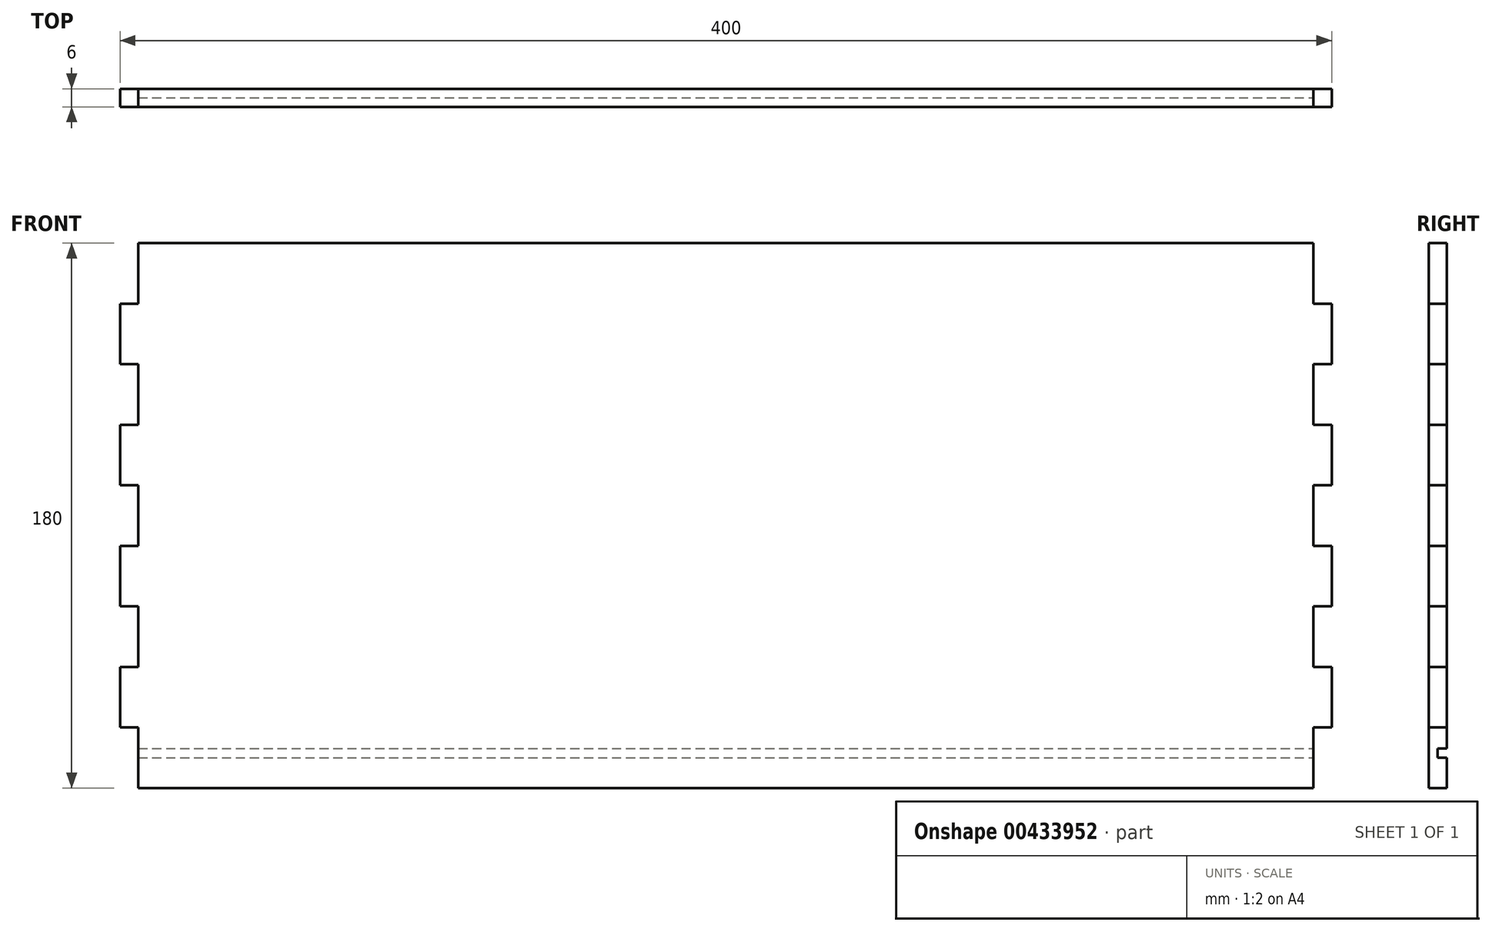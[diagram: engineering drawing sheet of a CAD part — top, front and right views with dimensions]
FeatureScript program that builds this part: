
annotation { "Feature Type Name" : "Feature", "Feature Type Description" : "" }
export const myFeature = defineFeature(function(context is Context, id is Id, definition is map)
    precondition{}
    {
        {
            var Q0;
            Q0=qCreatedBy(makeId("Top.planeOp"),FACE);
            var sketch = newSketch(context, id + "F0", { "sketchPlane" : qUnion([Q0])});
            skLineSegment(sketch, "E0.bottom", {"start": v(200, -3) * mm, "end": v(-200, -3) * mm});
            skLineSegment(sketch, "E0.top", {"start": v(200, 3) * mm, "end": v(-200, 3) * mm});
            skLineSegment(sketch, "E0.left", {"start": v(200, -3) * mm, "end": v(200, 3) * mm});
            skLineSegment(sketch, "E0.right", {"start": v(-200, -3) * mm, "end": v(-200, 3) * mm});
            skPoint(sketch, "E0.middle", {"position": v(0, 0) * mm});
            skSolve(sketch);
        }
        {
            var Q0;
            Q0=makeQuery(id+"F0.imprint","IMPRINT",FACE,{"disambiguationData":[TD([[makeQuery(id+"F0.imprint","IMPRINT",EDGE,{"derivedFrom":sQuery(id+"F0.wireOp",EDGE,"E0.bottom")}),-1.0]])]});
            extrude(context, id + "F1", {"entities" : qUnion([Q0]), "depth" : 180 * mm});
        }
        {
            var Q0;
            Q0=makeQuery(id+"F1.opExtrude","SWEPT_FACE",FACE,{"disambiguationData":[OSD([sQuery(id+"F0.wireOp",EDGE,"E0.left")])]});
            var sketch = newSketch(context, id + "F2", { "sketchPlane" : qUnion([Q0])});
            skLineSegment(sketch, "E1", {"start": v(3, 10) * mm, "end": v(0, 10) * mm});
            skLineSegment(sketch, "E2", {"start": v(3, 13) * mm, "end": v(3, 10) * mm});
            skLineSegment(sketch, "E3", {"start": v(0, 10) * mm, "end": v(0, 13) * mm});
            skLineSegment(sketch, "E4", {"start": v(0, 13) * mm, "end": v(3, 13) * mm});
            skSolve(sketch);
        }
        {
            var Q0;
            Q0=makeQuery(id+"F2.imprint","IMPRINT",FACE,{"disambiguationData":[TD([[makeQuery(id+"F2.imprint","IMPRINT",EDGE,{"derivedFrom":sQuery(id+"F2.wireOp",EDGE,"E1")}),-1.0]])]});
            extrude(context, id + "F3", {"entities" : qUnion([Q0]), "operationType" : NewBodyOperationType.REMOVE, "endBound" : BoundingType.THROUGH_ALL, "oppositeDirection" : true, "depth" : 25 * mm});
        }
        {
            var Q0;
            Q0=makeQuery(id+"F1.opExtrude","SWEPT_FACE",FACE,{"disambiguationData":[OSD([sQuery(id+"F0.wireOp",EDGE,"E0.bottom")])]});
            var sketch = newSketch(context, id + "F4", { "sketchPlane" : qUnion([Q0])});
            skLineSegment(sketch, "E5", {"start": v(-200, 0) * mm, "end": v(-194, 0) * mm});
            skLineSegment(sketch, "E6", {"start": v(-194, 0) * mm, "end": v(-194, 20) * mm});
            skLineSegment(sketch, "E7", {"start": v(-194, 20) * mm, "end": v(-200, 20) * mm});
            skLineSegment(sketch, "E8.1.0.0", {"start": v(-194, 60) * mm, "end": v(-200, 60) * mm});
            skLineSegment(sketch, "E8.1.0.1", {"start": v(-194, 40) * mm, "end": v(-194, 60) * mm});
            skLineSegment(sketch, "E8.1.0.2", {"start": v(-200, 40) * mm, "end": v(-194, 40) * mm});
            skLineSegment(sketch, "E8.2.0.0", {"start": v(-194, 100) * mm, "end": v(-200, 100) * mm});
            skLineSegment(sketch, "E8.2.0.1", {"start": v(-194, 80) * mm, "end": v(-194, 100) * mm});
            skLineSegment(sketch, "E8.2.0.2", {"start": v(-200, 80) * mm, "end": v(-194, 80) * mm});
            skLineSegment(sketch, "E8.3.0.0", {"start": v(-194, 140) * mm, "end": v(-200, 140) * mm});
            skLineSegment(sketch, "E8.3.0.1", {"start": v(-194, 120) * mm, "end": v(-194, 140) * mm});
            skLineSegment(sketch, "E8.3.0.2", {"start": v(-200, 120) * mm, "end": v(-194, 120) * mm});
            skLineSegment(sketch, "E8.4.0.0", {"start": v(-194, 180) * mm, "end": v(-200, 180) * mm});
            skLineSegment(sketch, "E8.4.0.1", {"start": v(-194, 160) * mm, "end": v(-194, 180) * mm});
            skLineSegment(sketch, "E8.4.0.2", {"start": v(-200, 160) * mm, "end": v(-194, 160) * mm});
            skLineSegment(sketch, "E8.direction1", {"start": v(-200, 20) * mm, "end": v(-200, 60) * mm, "construction": true});
            skLineSegment(sketch, "E9.MirrorCS", {"start": v(194, 60) * mm, "end": v(200, 60) * mm});
            skLineSegment(sketch, "E10.MirrorCS", {"start": v(194, 20) * mm, "end": v(200, 20) * mm});
            skLineSegment(sketch, "E11.MirrorCS", {"start": v(194, 180) * mm, "end": v(200, 180) * mm});
            skLineSegment(sketch, "E12.MirrorCS", {"start": v(200, 120) * mm, "end": v(194, 120) * mm});
            skLineSegment(sketch, "E13.MirrorCS", {"start": v(194, 140) * mm, "end": v(200, 140) * mm});
            skLineSegment(sketch, "E14.MirrorCS", {"start": v(200, 80) * mm, "end": v(194, 80) * mm});
            skLineSegment(sketch, "E15.MirrorCS", {"start": v(194, 100) * mm, "end": v(200, 100) * mm});
            skLineSegment(sketch, "E16.MirrorCS", {"start": v(200, 40) * mm, "end": v(194, 40) * mm});
            skLineSegment(sketch, "E17.MirrorCS", {"start": v(200, 0) * mm, "end": v(194, 0) * mm});
            skLineSegment(sketch, "E18.MirrorCS", {"start": v(200, 160) * mm, "end": v(194, 160) * mm});
            skLineSegment(sketch, "E19.MirrorCS", {"start": v(194, 120) * mm, "end": v(194, 140) * mm});
            skLineSegment(sketch, "E20.MirrorCS", {"start": v(194, 80) * mm, "end": v(194, 100) * mm});
            skLineSegment(sketch, "E21.MirrorCS", {"start": v(194, 40) * mm, "end": v(194, 60) * mm});
            skLineSegment(sketch, "E22.MirrorCS", {"start": v(194, 0) * mm, "end": v(194, 20) * mm});
            skLineSegment(sketch, "E23.MirrorCS", {"start": v(200, 20) * mm, "end": v(200, 60) * mm, "construction": true});
            skLineSegment(sketch, "E24.MirrorCS", {"start": v(194, 160) * mm, "end": v(194, 180) * mm});
            skSolve(sketch);
        }
        {
            var Q0;
            {var subQ0=sQuery(id+"F4.wireOp",EDGE,"E8.4.0.0");Q0=makeQuery(id+"F4.imprint","IMPRINT",FACE,{"disambiguationData":[TD([[makeQuery(id+"F4.imprint","IMPRINT",EDGE,{"derivedFrom":subQ0}),1.0]])]});}
            var Q1;
            {var subQ0=sQuery(id+"F4.wireOp",EDGE,"E8.3.0.0");Q1=makeQuery(id+"F4.imprint","IMPRINT",FACE,{"disambiguationData":[TD([[makeQuery(id+"F4.imprint","IMPRINT",EDGE,{"derivedFrom":subQ0}),1.0]])]});}
            var Q2;
            {var subQ0=sQuery(id+"F4.wireOp",EDGE,"E8.2.0.0");Q2=makeQuery(id+"F4.imprint","IMPRINT",FACE,{"disambiguationData":[TD([[makeQuery(id+"F4.imprint","IMPRINT",EDGE,{"derivedFrom":subQ0}),1.0]])]});}
            var Q3;
            {var subQ0=sQuery(id+"F4.wireOp",EDGE,"E8.1.0.0");Q3=makeQuery(id+"F4.imprint","IMPRINT",FACE,{"disambiguationData":[TD([[makeQuery(id+"F4.imprint","IMPRINT",EDGE,{"derivedFrom":subQ0}),1.0]])]});}
            var Q4;
            {var subQ0=sQuery(id+"F4.wireOp",EDGE,"E5");Q4=makeQuery(id+"F4.imprint","IMPRINT",FACE,{"disambiguationData":[TD([[makeQuery(id+"F4.imprint","IMPRINT",EDGE,{"derivedFrom":subQ0}),-1.0]])]});}
            var Q5;
            {var subQ0=sQuery(id+"F4.wireOp",EDGE,"E10.MirrorCS");Q5=makeQuery(id+"F4.imprint","IMPRINT",FACE,{"disambiguationData":[TD([[makeQuery(id+"F4.imprint","IMPRINT",EDGE,{"derivedFrom":subQ0}),-1.0]])]});}
            var Q6;
            {var subQ0=sQuery(id+"F4.wireOp",EDGE,"E9.MirrorCS");Q6=makeQuery(id+"F4.imprint","IMPRINT",FACE,{"disambiguationData":[TD([[makeQuery(id+"F4.imprint","IMPRINT",EDGE,{"derivedFrom":subQ0}),-1.0]])]});}
            var Q7;
            {var subQ0=sQuery(id+"F4.wireOp",EDGE,"E14.MirrorCS");Q7=makeQuery(id+"F4.imprint","IMPRINT",FACE,{"disambiguationData":[TD([[makeQuery(id+"F4.imprint","IMPRINT",EDGE,{"derivedFrom":subQ0}),-1.0]])]});}
            var Q8;
            {var subQ0=sQuery(id+"F4.wireOp",EDGE,"E12.MirrorCS");Q8=makeQuery(id+"F4.imprint","IMPRINT",FACE,{"disambiguationData":[TD([[makeQuery(id+"F4.imprint","IMPRINT",EDGE,{"derivedFrom":subQ0}),-1.0]])]});}
            var Q9;
            {var subQ0=sQuery(id+"F4.wireOp",EDGE,"E11.MirrorCS");Q9=makeQuery(id+"F4.imprint","IMPRINT",FACE,{"disambiguationData":[TD([[makeQuery(id+"F4.imprint","IMPRINT",EDGE,{"derivedFrom":subQ0}),-1.0]])]});}
            var Q10;
            {var subQ0=sQuery(id+"F4.wireOp",EDGE,"E11.MirrorCS");Q10=makeQuery(id+"F4.imprint","IMPRINT",FACE,{"disambiguationData":[TD([[makeQuery(id+"F4.imprint","IMPRINT",EDGE,{"derivedFrom":subQ0}),1.0]])]});}
            extrude(context, id + "F5", {"entities" : qUnion([Q0, Q1, Q2, Q3, Q4, Q5, Q6, Q7, Q8, Q9, Q10]), "operationType" : NewBodyOperationType.REMOVE, "endBound" : BoundingType.THROUGH_ALL, "oppositeDirection" : true, "depth" : 25 * mm});
        }
    });
